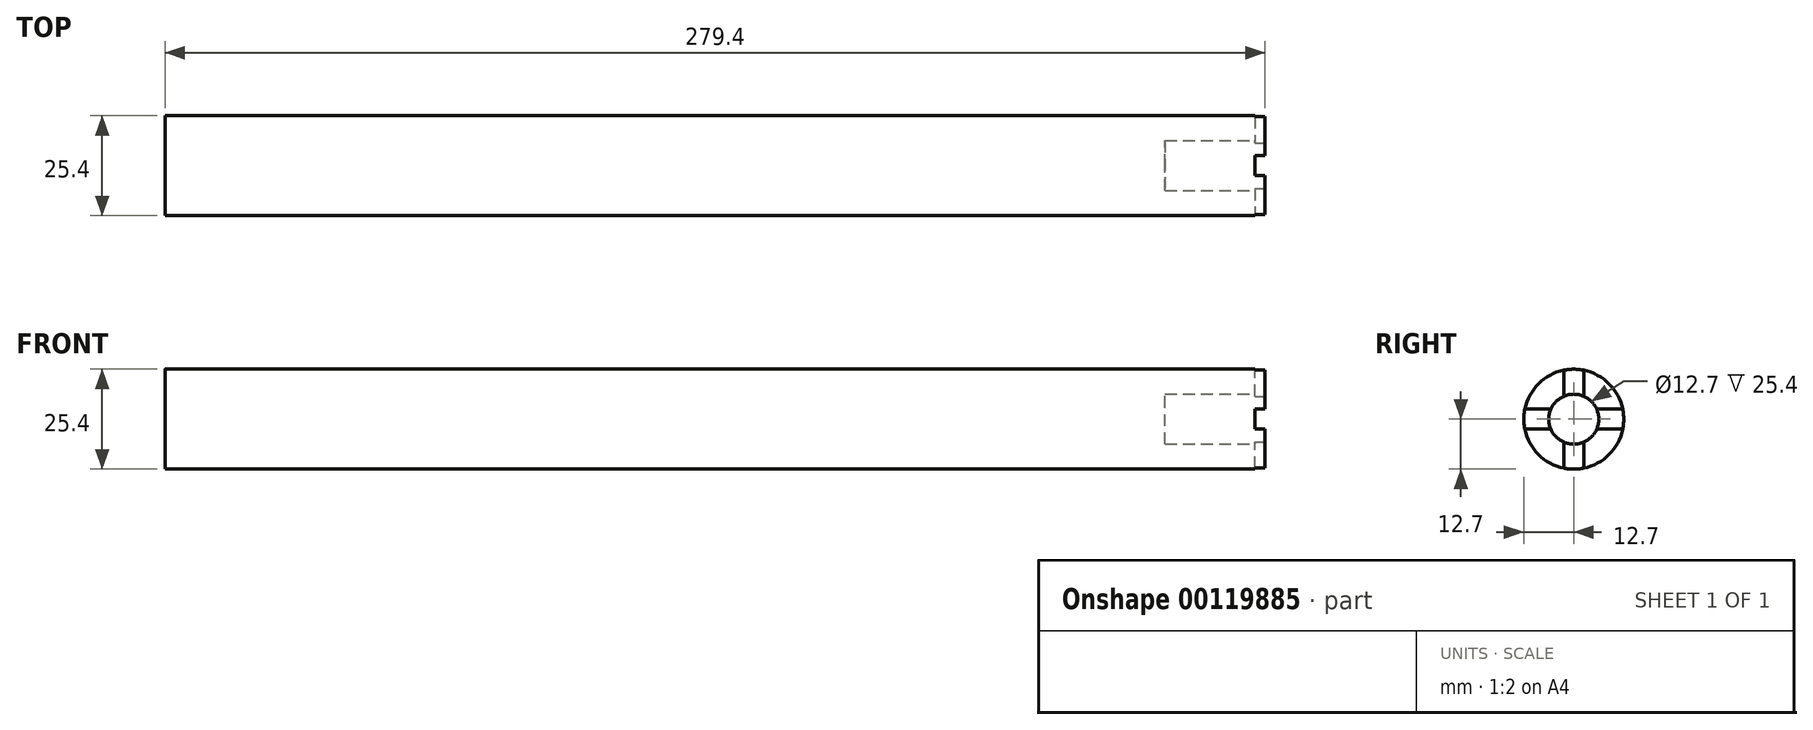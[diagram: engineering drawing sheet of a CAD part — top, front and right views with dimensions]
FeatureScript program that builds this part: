
annotation { "Feature Type Name" : "Feature", "Feature Type Description" : "" }
export const myFeature = defineFeature(function(context is Context, id is Id, definition is map)
    precondition{}
    {
        {
            var Q0;
            Q0=qCreatedBy(makeId("Right.planeOp"),FACE);
            var sketch = newSketch(context, id + "F0", { "sketchPlane" : qUnion([Q0])});
            skCircle(sketch, "E0", {"center": v(0, 0) * mm, "radius": 12.7 * mm});
            skSolve(sketch);
        }
        {
            var Q0;
            Q0=qCreatedBy(makeId("Front.planeOp"),FACE);
            var sketch = newSketch(context, id + "F1", { "sketchPlane" : qUnion([Q0])});
            skLineSegment(sketch, "E1", {"start": v(0, 0) * mm, "end": v(-279.4, 0) * mm});
            skSolve(sketch);
        }
        {
            var Q0;
            Q0=makeQuery(id+"F0.imprint","IMPRINT",FACE,{"disambiguationData":[TD([[makeQuery(id+"F0.imprint","IMPRINT",EDGE,{"derivedFrom":sQuery(id+"F0.wireOp",EDGE,"E0")}),1.0]])]});
            var Q1;
            Q1=sQuery(id+"F1.wireOp",EDGE,"E1");
            sweep(context, id + "F2", {"profiles" : qUnion([Q0]), "path" : qUnion([Q1])});
        }
        {
            var Q0;
            Q0=qCreatedBy(makeId("Top.planeOp"),FACE);
            var sketch = newSketch(context, id + "F3", { "sketchPlane" : qUnion([Q0])});
            skLineSegment(sketch, "E2.bottom", {"start": v(2.54, 2.54) * mm, "end": v(-2.54, 2.54) * mm});
            skLineSegment(sketch, "E2.top", {"start": v(2.54, -2.54) * mm, "end": v(-2.54, -2.54) * mm});
            skLineSegment(sketch, "E2.left", {"start": v(2.54, 2.54) * mm, "end": v(2.54, -2.54) * mm});
            skLineSegment(sketch, "E2.right", {"start": v(-2.54, 2.54) * mm, "end": v(-2.54, -2.54) * mm});
            skPoint(sketch, "E2.middle", {"position": v(0, 0) * mm});
            skSolve(sketch);
        }
        {
            var Q0;
            Q0 = qSketchRegion(id + "F3", true);
            extrude(context, id + "F4", {"entities" : qUnion([Q0]), "operationType" : NewBodyOperationType.REMOVE, "endBound" : BoundingType.SYMMETRIC, "oppositeDirection" : true, "depth" : 50.8 * mm});
        }
        {
            var Q0;
            Q0=qCreatedBy(makeId("Front.planeOp"),FACE);
            var sketch = newSketch(context, id + "F5", { "sketchPlane" : qUnion([Q0])});
            skLineSegment(sketch, "E3.bottom", {"start": v(2.54, 2.54) * mm, "end": v(-2.54, 2.54) * mm});
            skLineSegment(sketch, "E3.top", {"start": v(2.54, -2.54) * mm, "end": v(-2.54, -2.54) * mm});
            skLineSegment(sketch, "E3.left", {"start": v(2.54, 2.54) * mm, "end": v(2.54, -2.54) * mm});
            skLineSegment(sketch, "E3.right", {"start": v(-2.54, 2.54) * mm, "end": v(-2.54, -2.54) * mm});
            skPoint(sketch, "E3.middle", {"position": v(0, 0) * mm});
            skSolve(sketch);
        }
        {
            var Q0;
            Q0 = qSketchRegion(id + "F5", true);
            extrude(context, id + "F6", {"entities" : qUnion([Q0]), "operationType" : NewBodyOperationType.REMOVE, "endBound" : BoundingType.SYMMETRIC, "oppositeDirection" : true, "depth" : 50.8 * mm});
        }
        {
            var Q0;
            Q0=qCreatedBy(makeId("Right.planeOp"),FACE);
            var sketch = newSketch(context, id + "F7", { "sketchPlane" : qUnion([Q0])});
            skCircle(sketch, "E4", {"center": v(0, 0) * mm, "radius": 6.35 * mm});
            skSolve(sketch);
        }
        {
            var Q0;
            Q0 = qSketchRegion(id + "F7", true);
            extrude(context, id + "F8", {"entities" : qUnion([Q0]), "operationType" : NewBodyOperationType.REMOVE, "oppositeDirection" : true, "depth" : 25.4 * mm});
        }
    });
